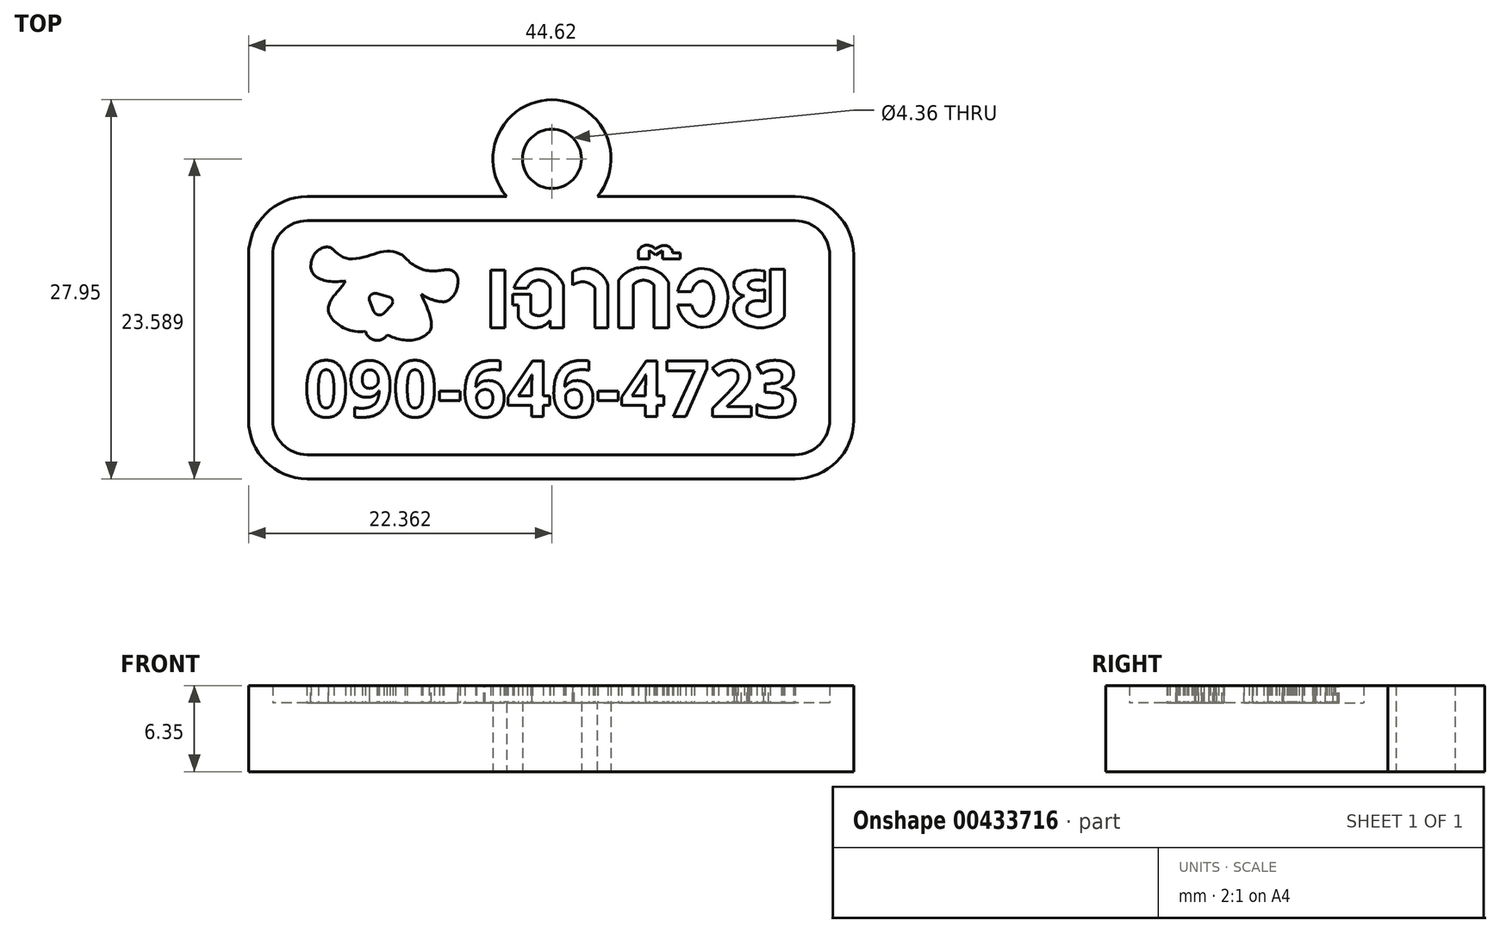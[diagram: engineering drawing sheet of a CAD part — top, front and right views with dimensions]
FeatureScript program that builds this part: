
annotation { "Feature Type Name" : "Feature", "Feature Type Description" : "" }
export const myFeature = defineFeature(function(context is Context, id is Id, definition is map)
    precondition{}
    {
        {
            var Q0;
            Q0=qCreatedBy(makeId("Top.planeOp"),FACE);
            var sketch = newSketch(context, id + "F0", { "sketchPlane" : qUnion([Q0])});
            skLineSegment(sketch, "E0.bottom", {"start": v(-18.17, -4.42) * mm, "end": v(17.82, -4.42) * mm});
            skLineSegment(sketch, "E0.top", {"start": v(-18.17, -21.67) * mm, "end": v(17.82, -21.67) * mm});
            skLineSegment(sketch, "E0.left", {"start": v(-20.7, -6.96) * mm, "end": v(-20.7, -19.13) * mm});
            skLineSegment(sketch, "E0.right", {"start": v(20.36, -6.96) * mm, "end": v(20.36, -19.13) * mm});
            skArc(sketch, "E1.filletArc", {"start": v(-18.17, -4.42) * mm, "mid": v(-19.96, -5.16) * mm, "end": v(-20.7, -6.96) * mm});
            skArc(sketch, "E2.filletArc", {"start": v(20.36, -6.96) * mm, "mid": v(19.61, -5.16) * mm, "end": v(17.82, -4.42) * mm});
            skArc(sketch, "E3.filletArc", {"start": v(17.82, -21.67) * mm, "mid": v(19.61, -20.93) * mm, "end": v(20.36, -19.13) * mm});
            skArc(sketch, "E4.filletArc", {"start": v(-20.7, -19.13) * mm, "mid": v(-19.96, -20.93) * mm, "end": v(-18.17, -21.67) * mm});
            skArc(sketch, "E5.0", {"start": v(-18.17, -2.64) * mm, "mid": v(-21.22, -3.9) * mm, "end": v(-22.48, -6.96) * mm});
            skLineSegment(sketch, "E5.1", {"start": v(-22.48, -6.96) * mm, "end": v(-22.48, -19.13) * mm});
            skLineSegment(sketch, "E5.2", {"start": v(-18.17, -2.64) * mm, "end": v(17.82, -2.64) * mm});
            skArc(sketch, "E5.3", {"start": v(-22.48, -19.13) * mm, "mid": v(-21.22, -22.18) * mm, "end": v(-18.17, -23.45) * mm});
            skArc(sketch, "E5.4", {"start": v(22.14, -6.96) * mm, "mid": v(20.87, -3.9) * mm, "end": v(17.82, -2.64) * mm});
            skLineSegment(sketch, "E5.5", {"start": v(22.14, -6.96) * mm, "end": v(22.14, -19.13) * mm});
            skArc(sketch, "E5.6", {"start": v(17.82, -23.45) * mm, "mid": v(20.87, -22.18) * mm, "end": v(22.14, -19.13) * mm});
            skLineSegment(sketch, "E5.7", {"start": v(-18.17, -23.45) * mm, "end": v(17.82, -23.45) * mm});
            skCircle(sketch, "E6", {"center": v(-0.12, 0.14) * mm, "radius": 4.36 * mm});
            skCircle(sketch, "E7", {"center": v(-0.12, 0.14) * mm, "radius": 2.18 * mm});
            skSolve(sketch);
        }
        {
            var Q0;
            Q0 = qSketchRegion(id + "F0", true);
            extrude(context, id + "F1", {"entities" : qUnion([Q0]), "depth" : 6.35 * mm});
        }
        {
            var Q0;
            Q0=qCreatedBy(makeId("Top.planeOp"),FACE);
            var sketch = newSketch(context, id + "F2", { "sketchPlane" : qUnion([Q0])});
            skArc(sketch, "E8.0", {"start": v(-18.17, -2.64) * mm, "mid": v(-21.22, -3.9) * mm, "end": v(-22.48, -6.96) * mm});
            skLineSegment(sketch, "E8.1", {"start": v(-22.48, -6.96) * mm, "end": v(-22.48, -19.13) * mm});
            skLineSegment(sketch, "E8.2", {"start": v(-18.17, -2.64) * mm, "end": v(17.82, -2.64) * mm});
            skArc(sketch, "E8.3", {"start": v(-22.48, -19.13) * mm, "mid": v(-21.22, -22.18) * mm, "end": v(-18.17, -23.45) * mm});
            skArc(sketch, "E8.4", {"start": v(22.13, -6.96) * mm, "mid": v(20.87, -3.9) * mm, "end": v(17.82, -2.64) * mm});
            skLineSegment(sketch, "E8.5", {"start": v(22.13, -6.96) * mm, "end": v(22.13, -19.13) * mm});
            skArc(sketch, "E8.6", {"start": v(17.82, -23.45) * mm, "mid": v(20.87, -22.18) * mm, "end": v(22.13, -19.13) * mm});
            skLineSegment(sketch, "E8.7", {"start": v(-18.17, -23.45) * mm, "end": v(17.82, -23.45) * mm});
            skSolve(sketch);
        }
        {
            var Q0;
            Q0 = qSketchRegion(id + "F2", true);
            extrude(context, id + "F3", {"entities" : qUnion([Q0]), "operationType" : NewBodyOperationType.ADD, "depth" : 5.08 * mm});
        }
        {
            var Q0;
            Q0=qCreatedBy(makeId("Top.planeOp"),FACE);
            var sketch = newSketch(context, id + "F4", { "sketchPlane" : qUnion([Q0])});
            skFitSpline(sketch, "E9", {"points": [v(-16.3, -6.51) * mm, v(-15.18, -7.22) * mm, v(-13.56, -6.98) * mm, v(-12.2, -6.67) * mm, v(-10.94, -7.13) * mm], "startDerivative": vector(4.65, -4.12) * mm, "endDerivative": vector(4.4, -4.2) * mm});
            skFitSpline(sketch, "E10", {"points": [v(-10.94, -7.13) * mm, v(-8.1, -8.05) * mm], "startDerivative": vector(2.64, -3.02) * mm, "endDerivative": vector(2.8, 0.56) * mm});
            skFitSpline(sketch, "E11", {"points": [v(-8.1, -8.05) * mm, v(-7.05, -8.8) * mm], "startDerivative": vector(2.13, 0.38) * mm, "endDerivative": vector(0.08, -1.45) * mm});
            skFitSpline(sketch, "E12", {"points": [v(-7.05, -8.8) * mm, v(-8.15, -10.4) * mm], "startDerivative": vector(0.08, -2.77) * mm, "endDerivative": vector(-1.6, 0.13) * mm});
            skFitSpline(sketch, "E13", {"points": [v(-8.15, -10.4) * mm, v(-9.76, -9.85) * mm], "startDerivative": vector(-1.75, 0.03) * mm, "endDerivative": vector(-1.47, 0.84) * mm});
            skFitSpline(sketch, "E14", {"points": [v(-9.76, -9.85) * mm, v(-9.18, -12.63) * mm], "startDerivative": vector(1.27, -2.9) * mm, "endDerivative": vector(-1.5, -1.55) * mm});
            skFitSpline(sketch, "E15", {"points": [v(-9.18, -12.63) * mm, v(-12.27, -12.85) * mm], "startDerivative": vector(-2.39, -2.6) * mm, "endDerivative": vector(-3, 1.42) * mm});
            skArc(sketch, "E16", {"start": v(-13.86, -12.58) * mm, "mid": v(-13.16, -13.23) * mm, "end": v(-12.27, -12.85) * mm});
            skFitSpline(sketch, "E17", {"points": [v(-13.86, -12.58) * mm, v(-16.6, -10.9) * mm], "startDerivative": vector(-4.62, -0.69) * mm, "endDerivative": vector(0.3, 2.16) * mm});
            skFitSpline(sketch, "E18", {"points": [v(-16.6, -10.9) * mm, v(-15.35, -8.86) * mm], "startDerivative": vector(0.1, 2.44) * mm, "endDerivative": vector(0.91, 1.96) * mm});
            skFitSpline(sketch, "E19", {"points": [v(-15.35, -8.86) * mm, v(-17.89, -7.63) * mm], "startDerivative": vector(-4.55, -0.76) * mm, "endDerivative": vector(0.48, 2.85) * mm});
            skFitSpline(sketch, "E20", {"points": [v(-17.89, -7.63) * mm, v(-16.3, -6.51) * mm], "startDerivative": vector(0.28, 3.13) * mm, "endDerivative": vector(1.4, -1.25) * mm});
            skLineSegment(sketch, "E21", {"start": v(-13.05, -9.8) * mm, "end": v(-12.05, -10.07) * mm});
            skLineSegment(sketch, "E22", {"start": v(-11.95, -10.63) * mm, "end": v(-12.52, -11.24) * mm});
            skLineSegment(sketch, "E23", {"start": v(-13.26, -11.1) * mm, "end": v(-13.6, -10.25) * mm});
            skArc(sketch, "E24", {"start": v(-13.05, -9.8) * mm, "mid": v(-13.44, -9.88) * mm, "end": v(-13.6, -10.25) * mm});
            skArc(sketch, "E25", {"start": v(-11.95, -10.63) * mm, "mid": v(-11.86, -10.33) * mm, "end": v(-12.05, -10.07) * mm});
            skArc(sketch, "E26", {"start": v(-13.26, -11.1) * mm, "mid": v(-12.92, -11.37) * mm, "end": v(-12.52, -11.24) * mm});
            skLineSegment(sketch, "E27.bottom", {"start": v(-4.63, -8.05) * mm, "end": v(-3.58, -8.05) * mm});
            skLineSegment(sketch, "E27.top", {"start": v(-4.63, -12.33) * mm, "end": v(-3.58, -12.33) * mm});
            skLineSegment(sketch, "E27.left", {"start": v(-4.63, -8.05) * mm, "end": v(-4.63, -12.33) * mm});
            skLineSegment(sketch, "E27.right", {"start": v(-3.58, -8.05) * mm, "end": v(-3.58, -12.33) * mm});
            skLineSegment(sketch, "E28", {"start": v(-2.62, -11.52) * mm, "end": v(-2.62, -10.63) * mm});
            skLineSegment(sketch, "E29", {"start": v(-2.62, -10.63) * mm, "end": v(-3, -10.63) * mm});
            skLineSegment(sketch, "E30", {"start": v(-3, -10.63) * mm, "end": v(-3, -9.84) * mm});
            skLineSegment(sketch, "E31", {"start": v(-3, -9.84) * mm, "end": v(-1.67, -9.84) * mm});
            skLineSegment(sketch, "E32", {"start": v(-1.67, -9.84) * mm, "end": v(-1.67, -11.2) * mm});
            skLineSegment(sketch, "E33", {"start": v(-0.26, -9.4) * mm, "end": v(-0.26, -10.83) * mm});
            skLineSegment(sketch, "E34", {"start": v(0.74, -9.18) * mm, "end": v(0.74, -12.33) * mm});
            skLineSegment(sketch, "E35", {"start": v(0.74, -12.33) * mm, "end": v(-0.26, -12.33) * mm});
            skLineSegment(sketch, "E36", {"start": v(-0.26, -12.33) * mm, "end": v(-0.26, -11.79) * mm});
            skLineSegment(sketch, "E37", {"start": v(-1.92, -9.4) * mm, "end": v(-2.9, -9.4) * mm});
            skArc(sketch, "E38", {"start": v(-0.26, -9.4) * mm, "mid": v(-1.1, -8.8) * mm, "end": v(-1.92, -9.4) * mm});
            skArc(sketch, "E39", {"start": v(0.74, -9.18) * mm, "mid": v(-1.17, -7.97) * mm, "end": v(-2.9, -9.4) * mm});
            skArc(sketch, "E40", {"start": v(-1.67, -11.2) * mm, "mid": v(-0.86, -11.4) * mm, "end": v(-0.26, -10.83) * mm});
            skArc(sketch, "E41", {"start": v(-2.62, -11.52) * mm, "mid": v(-1.51, -12.3) * mm, "end": v(-0.26, -11.79) * mm});
            skLineSegment(sketch, "E42", {"start": v(3.04, -9.37) * mm, "end": v(3.04, -12.33) * mm});
            skLineSegment(sketch, "E43", {"start": v(3.04, -12.33) * mm, "end": v(4.01, -12.33) * mm});
            skLineSegment(sketch, "E44", {"start": v(4.01, -12.33) * mm, "end": v(4.01, -9.18) * mm});
            skLineSegment(sketch, "E45", {"start": v(1.41, -8.2) * mm, "end": v(1.41, -9.18) * mm});
            skArc(sketch, "E46", {"start": v(3.04, -9.37) * mm, "mid": v(2.27, -8.94) * mm, "end": v(1.41, -9.18) * mm});
            skArc(sketch, "E47", {"start": v(4.01, -9.18) * mm, "mid": v(2.96, -8.04) * mm, "end": v(1.41, -8.2) * mm});
            skLineSegment(sketch, "E48", {"start": v(4.8, -8.8) * mm, "end": v(4.8, -12.33) * mm});
            skLineSegment(sketch, "E49", {"start": v(4.8, -12.33) * mm, "end": v(5.86, -12.33) * mm});
            skLineSegment(sketch, "E50", {"start": v(5.86, -12.33) * mm, "end": v(5.86, -9.17) * mm});
            skLineSegment(sketch, "E51", {"start": v(7.4, -9.17) * mm, "end": v(7.4, -12.33) * mm});
            skLineSegment(sketch, "E52", {"start": v(7.4, -12.33) * mm, "end": v(8.47, -12.33) * mm});
            skLineSegment(sketch, "E53", {"start": v(8.47, -12.33) * mm, "end": v(8.47, -8.95) * mm});
            skArc(sketch, "E54", {"start": v(7.4, -9.17) * mm, "mid": v(6.63, -8.81) * mm, "end": v(5.86, -9.17) * mm});
            skArc(sketch, "E55", {"start": v(8.47, -8.95) * mm, "mid": v(6.68, -7.87) * mm, "end": v(4.8, -8.8) * mm});
            skLineSegment(sketch, "E56", {"start": v(9.14, -10.64) * mm, "end": v(10.17, -10.64) * mm});
            skPoint(sketch, "E56.startSnap0", {"position": v(8.47, -10.64) * mm});
            skLineSegment(sketch, "E57", {"start": v(9.14, -9.64) * mm, "end": v(10.17, -9.64) * mm});
            skFitSpline(sketch, "E58", {"points": [v(10.17, -9.64) * mm, v(11.74, -9.64) * mm], "startDerivative": vector(0.97, 3.14) * mm, "endDerivative": vector(0.66, -3.05) * mm});
            skFitSpline(sketch, "E59", {"points": [v(10.17, -10.64) * mm, v(11.74, -10.64) * mm], "startDerivative": vector(0.76, -3.26) * mm, "endDerivative": vector(0.73, 3.35) * mm});
            skFitSpline(sketch, "E60", {"points": [v(11.74, -9.64) * mm, v(11.74, -10.64) * mm], "startDerivative": vector(0.3, -0.94) * mm, "endDerivative": vector(-0.27, -1.06) * mm});
            skFitSpline(sketch, "E61", {"points": [v(9.14, -9.64) * mm, v(12.85, -10.06) * mm], "startDerivative": vector(2.05, 7.74) * mm, "endDerivative": vector(0.3, -7.31) * mm});
            skFitSpline(sketch, "E62", {"points": [v(9.14, -10.64) * mm, v(12.85, -10.06) * mm], "startDerivative": vector(1.2, -6.92) * mm, "endDerivative": vector(-0.18, 8.58) * mm});
            skLineSegment(sketch, "E63", {"start": v(17.03, -11.5) * mm, "end": v(17.03, -8.01) * mm});
            skLineSegment(sketch, "E64", {"start": v(17.03, -8.01) * mm, "end": v(15.98, -8.01) * mm});
            skLineSegment(sketch, "E65", {"start": v(15.98, -8.01) * mm, "end": v(15.98, -11.16) * mm});
            skLineSegment(sketch, "E66", {"start": v(15.55, -8.13) * mm, "end": v(15.55, -8.89) * mm});
            skLineSegment(sketch, "E67", {"start": v(15.55, -9.48) * mm, "end": v(15.55, -10.38) * mm});
            skFitSpline(sketch, "E68", {"points": [v(15.55, -9.48) * mm, v(15.55, -8.89) * mm], "startDerivative": vector(-4.74, -1.18) * mm, "endDerivative": vector(4.86, -1.33) * mm});
            skFitSpline(sketch, "E69", {"points": [v(15.55, -8.13) * mm, v(14.05, -9.96) * mm], "startDerivative": vector(-6.95, 1.39) * mm, "endDerivative": vector(4.3, -1.2) * mm});
            skFitSpline(sketch, "E70", {"points": [v(15.55, -10.38) * mm, v(14.27, -11.16) * mm], "startDerivative": vector(-2.48, 0.51) * mm, "endDerivative": vector(0.51, -2.2) * mm});
            skFitSpline(sketch, "E71", {"points": [v(14.05, -9.96) * mm, v(13.43, -11.5) * mm], "startDerivative": vector(-2.42, -0.97) * mm, "endDerivative": vector(0.9, -2.15) * mm});
            skArc(sketch, "E72", {"start": v(14.27, -11.16) * mm, "mid": v(15.13, -11.5) * mm, "end": v(15.98, -11.16) * mm});
            skArc(sketch, "E73", {"start": v(13.43, -11.5) * mm, "mid": v(15.23, -12.32) * mm, "end": v(17.03, -11.5) * mm});
            skLineSegment(sketch, "E74", {"start": v(6.26, -6.61) * mm, "end": v(6.26, -7.23) * mm});
            skLineSegment(sketch, "E75", {"start": v(6.26, -7.23) * mm, "end": v(7.04, -7.23) * mm});
            skLineSegment(sketch, "E76", {"start": v(7.04, -7.23) * mm, "end": v(7.04, -6.61) * mm});
            skLineSegment(sketch, "E77", {"start": v(7.04, -6.61) * mm, "end": v(7.52, -6.95) * mm});
            skLineSegment(sketch, "E78", {"start": v(7.52, -6.95) * mm, "end": v(8.05, -6.64) * mm});
            skLineSegment(sketch, "E79", {"start": v(8.05, -6.64) * mm, "end": v(8.05, -7.23) * mm});
            skLineSegment(sketch, "E80", {"start": v(8.05, -7.23) * mm, "end": v(9.34, -7.23) * mm});
            skLineSegment(sketch, "E81", {"start": v(9.34, -7.23) * mm, "end": v(9.34, -6.8) * mm});
            skLineSegment(sketch, "E82", {"start": v(9.34, -6.8) * mm, "end": v(8.75, -6.8) * mm});
            skFitSpline(sketch, "E83", {"points": [v(6.26, -6.61) * mm, v(7.52, -6.5) * mm], "startDerivative": vector(1.27, 1.81) * mm, "endDerivative": vector(1.18, -0.88) * mm});
            skFitSpline(sketch, "E84", {"points": [v(7.52, -6.5) * mm, v(8.75, -6.61) * mm], "startDerivative": vector(1.48, 1.03) * mm, "endDerivative": vector(0.94, -1.48) * mm});
            skLineSegment(sketch, "E85", {"start": v(8.75, -6.61) * mm, "end": v(8.75, -6.8) * mm});
            skText(sketch, "E86", { "text": "090-646-4723", "fontName": "OpenSans-Bold.ttf"});
            const initialGuessF4  = {"E86": [-0.0184, -0.01887, 1, 0, 0.00413]};
            skSetInitialGuess(sketch, initialGuessF4);
            skSolve(sketch);
        }
        {
            var Q0;
            Q0 = qSketchRegion(id + "F4", true);
            extrude(context, id + "F5", {"entities" : qUnion([Q0]), "operationType" : NewBodyOperationType.ADD, "depth" : 6.35 * mm});
        }
    });
